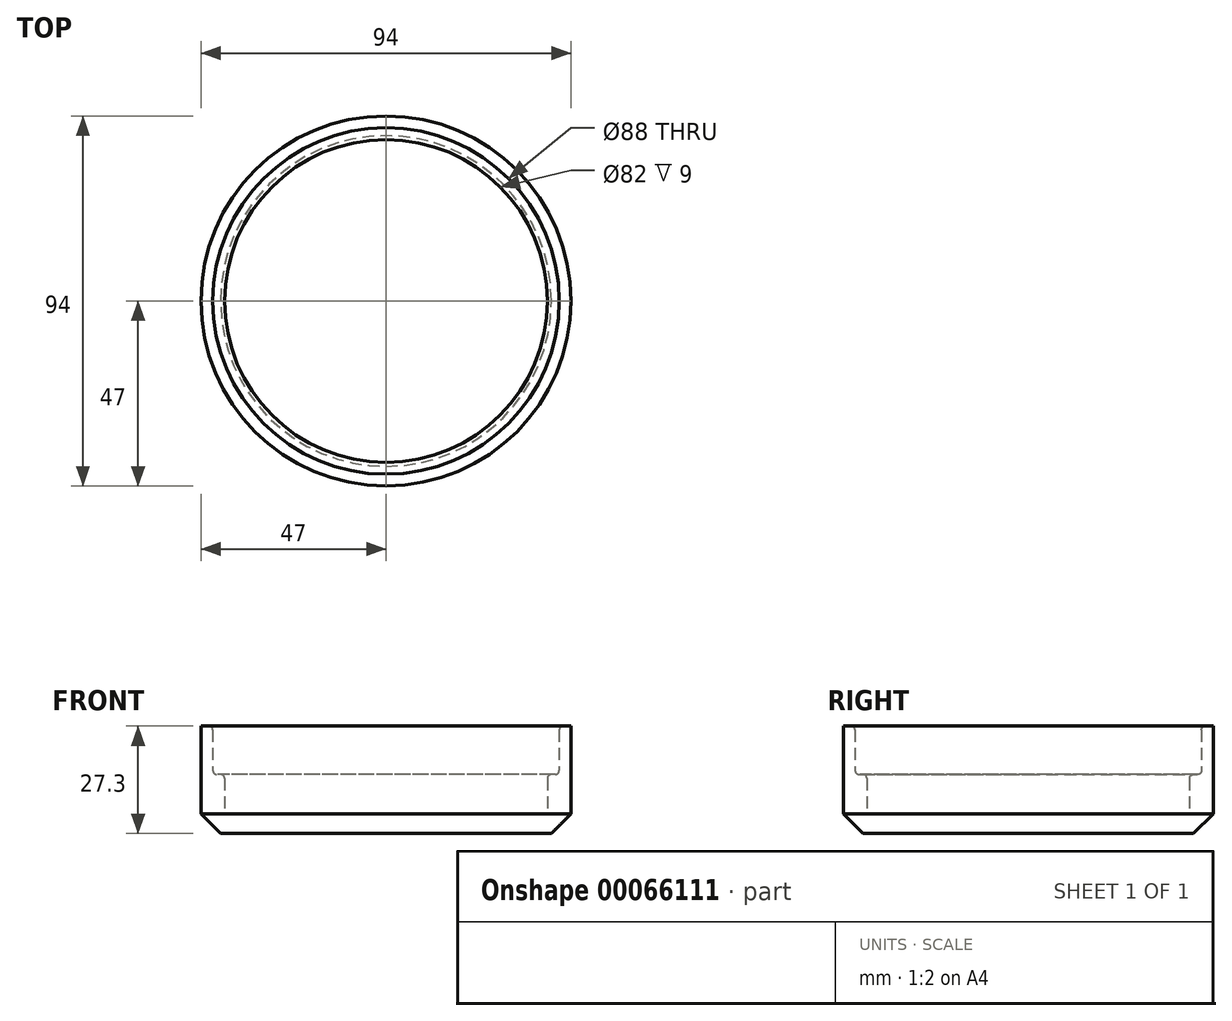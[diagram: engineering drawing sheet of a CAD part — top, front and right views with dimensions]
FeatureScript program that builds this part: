
annotation { "Feature Type Name" : "Feature", "Feature Type Description" : "" }
export const myFeature = defineFeature(function(context is Context, id is Id, definition is map)
    precondition{}
    {
        {
            var Q0;
            Q0=qCreatedBy(makeId("Top.planeOp"),FACE);
            var sketch = newSketch(context, id + "F0", { "sketchPlane" : qUnion([Q0])});
            skCircle(sketch, "E0", {"center": v(0, 0) * mm, "radius": 41 * mm});
            skCircle(sketch, "E1", {"center": v(0, 0) * mm, "radius": 44 * mm});
            skCircle(sketch, "E2", {"center": v(0, 0) * mm, "radius": 47 * mm});
            skSolve(sketch);
        }
        {
            var Q0;
            Q0 = qSketchRegion(id + "F0", true);
            extrude(context, id + "F1", {"entities" : qUnion([Q0]), "depth" : 22.3 * mm});
        }
        {
            var Q0;
            Q0=makeQuery(id+"F0.imprint","IMPRINT",FACE,{"disambiguationData":[TD([[makeQuery(id+"F0.imprint","IMPRINT",EDGE,{"derivedFrom":sQuery(id+"F0.wireOp",EDGE,"E0")}),-1.0]])]});
            extrude(context, id + "F2", {"entities" : qUnion([Q0]), "operationType" : NewBodyOperationType.ADD, "depth" : 10 * mm});
        }
        {
            var Q0;
            Q0=makeQuery(id+"F0.imprint","IMPRINT",FACE,{"disambiguationData":[TD([[makeQuery(id+"F0.imprint","IMPRINT",EDGE,{"derivedFrom":sQuery(id+"F0.wireOp",EDGE,"E0")}),1.0]])]});
            var Q1;
            Q1=makeQuery(id+"F0.imprint","IMPRINT",FACE,{"disambiguationData":[TD([[makeQuery(id+"F0.imprint","IMPRINT",EDGE,{"derivedFrom":sQuery(id+"F0.wireOp",EDGE,"E0")}),-1.0]])]});
            var Q2;
            Q2=makeQuery(id+"F0.imprint","IMPRINT",FACE,{"disambiguationData":[TD([[makeQuery(id+"F0.imprint","IMPRINT",EDGE,{"derivedFrom":sQuery(id+"F0.wireOp",EDGE,"E1")}),-1.0]])]});
            extrude(context, id + "F3", {"entities" : qUnion([Q0, Q1, Q2]), "operationType" : NewBodyOperationType.ADD, "oppositeDirection" : true, "depth" : 5 * mm});
        }
        {
            var Q0;
            Q0=makeQuery(id+"F1.opExtrude","CAP_EDGE",EDGE,{"disambiguationData":[OSD([sQuery(id+"F0.wireOp",EDGE,"E1")])],"isStart":false});
            var Q1;
            Q1=makeQuery(id+"F2.opExtrude","CAP_FACE",FACE,{"disambiguationData":[OSD([sQuery(id+"F0.wireOp",EDGE,"E0"),sQuery(id+"F0.wireOp",EDGE,"E1")])],"isStart":false});
            var Q2;
            Q2=makeQuery(id+"F2.opExtrude","CAP_EDGE",EDGE,{"disambiguationData":[OSD([sQuery(id+"F0.wireOp",EDGE,"E0")])],"isStart":true});
            fillet(context, id + "F4", {"entities" : qUnion([Q0, Q1, Q2]), "radius" : 1 * mm, "tangentPropagation" : true, "allowEdgeOverflow" : false});
        }
        {
            var Q0;
            Q0=makeQuery(id+"F3.opExtrude","CAP_EDGE",EDGE,{"disambiguationData":[OSD([sQuery(id+"F0.wireOp",EDGE,"E2")])],"isStart":false});
            chamfer(context, id + "F5", {"entities" : qUnion([Q0]), "width" : 5 * mm, "tangentPropagation" : true});
        }
    });
